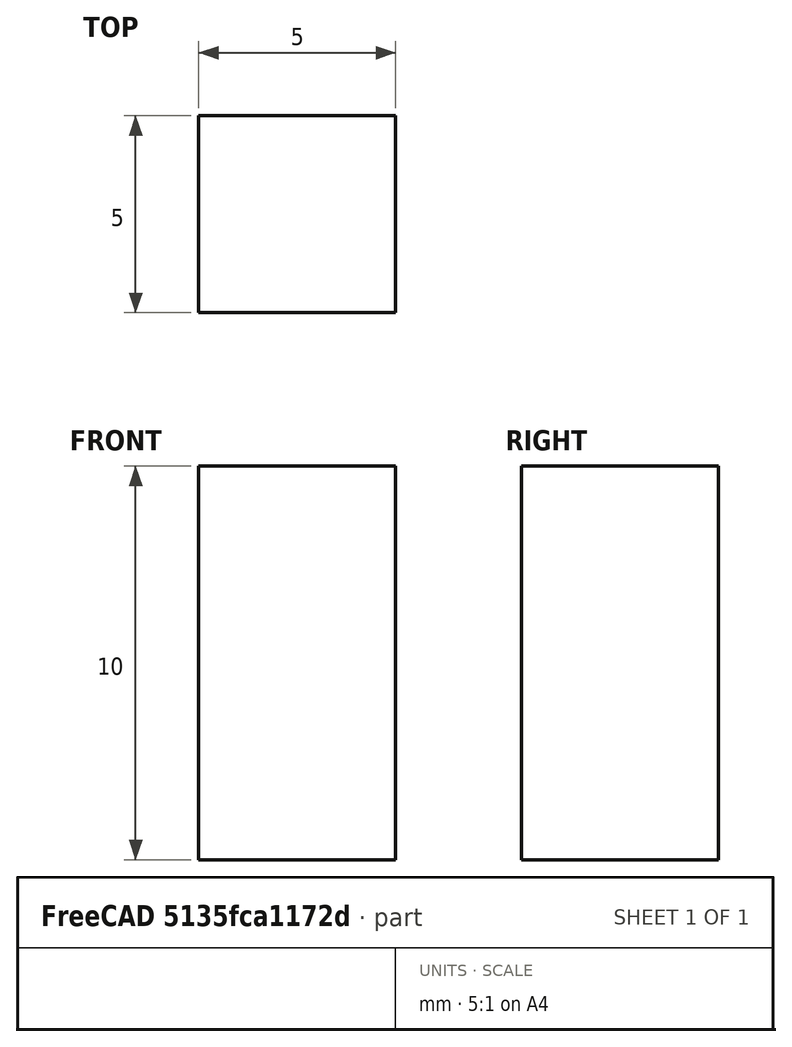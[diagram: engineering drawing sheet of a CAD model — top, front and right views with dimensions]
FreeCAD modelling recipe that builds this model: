
FCSTD DOCUMENT  (FreeCAD 1.1R44795 (Git))
Label: poly-xtal-5x5x10mm
License: All rights reserved
LicenseURL: https://en.wikipedia.org/wiki/All_rights_reserved
objects: App::Point×1, Sketcher::SketchObject×1, PartDesign::Pad×1, PartDesign::Body×1
note: 6 computed .brp shape members not serialized (recipe doc carries the construction recipe); baked Part::Feature solids carry a one-line shape summary decoded from their .brp

FEATURE [App::Point] Origin001
  Role = Origin
FEATURE [Sketcher::SketchObject] Sketch
  ArcFitTolerance = 1e-06
  AttachmentSupport = -> [Origin]
  ExternalTypes = [0]
  FullyConstrained = true
  MakeInternals = false
  MapMode = 5
  _ExternalGeoVersion = 1
  sketch-geometry (5):
    g0: LineSegment StartX=-2.5 StartY=-2.5 StartZ=0 EndX=2.5 EndY=-2.5 EndZ=0
    g1: LineSegment StartX=2.5 StartY=-2.5 StartZ=0 EndX=2.5 EndY=2.5 EndZ=0
    g2: LineSegment StartX=2.5 StartY=2.5 StartZ=0 EndX=-2.5 EndY=2.5 EndZ=0
    g3: LineSegment StartX=-2.5 StartY=2.5 StartZ=0 EndX=-2.5 EndY=-2.5 EndZ=0
    g4: GeomPoint [constr] X=0 Y=0 Z=0
  constraints (12):
    c: Coincident(g0,g1)
    c: Coincident(g1,g2)
    c: Coincident(g2,g3)
    c: Coincident(g3,g0)
    c: Horizontal(g0)
    c: Horizontal(g2)
    c: Vertical(g1)
    c: Vertical(g3)
    c: Symmetric(g2,g0,g4)
    c: Distance(g1,g3) = 5
    c: Distance(g0,g2) = 5
    c: Coincident(g4,g-1)
FEATURE [PartDesign::Pad] Pad
  Direction = (0,0,1)
  Length = 10
  Length2 = 10
  Profile = -> Sketch
  ReferenceAxis = -> Sketch [N_Axis]
  Refine = true
  SideType = 0
  Suppressed = false
  Type = 0
  Type2 = 0
FEATURE [PartDesign::Body] Body
  AllowCompound = true
  Group = -> [Sketch,Pad]
  Origin = -> Origin
  Tip = -> Pad
